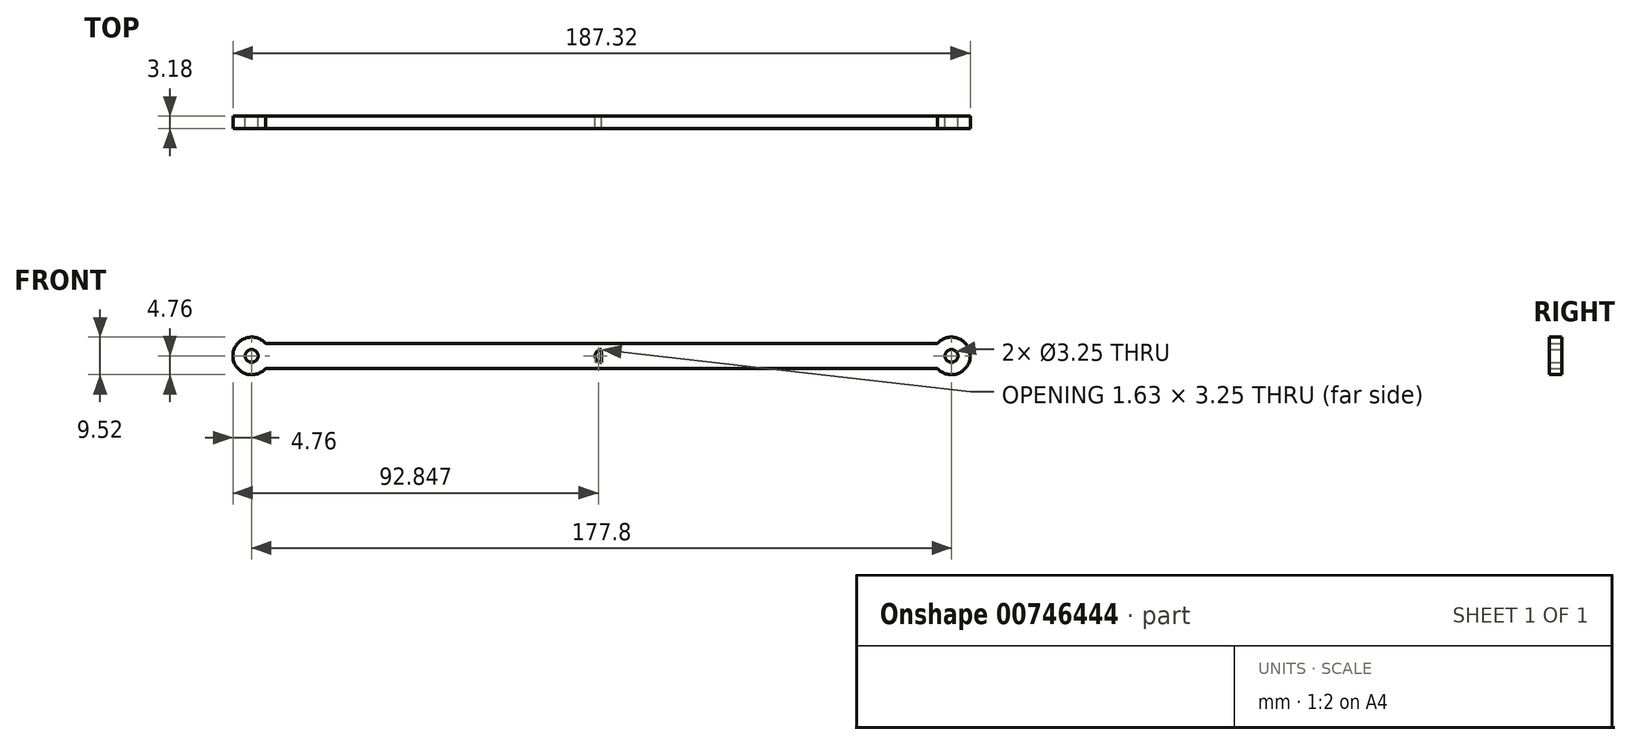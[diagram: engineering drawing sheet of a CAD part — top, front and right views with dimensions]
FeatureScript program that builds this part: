
annotation { "Feature Type Name" : "Feature", "Feature Type Description" : "" }
export const myFeature = defineFeature(function(context is Context, id is Id, definition is map)
    precondition{}
    {
        {
            var Q0;
            Q0=qCreatedBy(makeId("Front.planeOp"),FACE);
            var sketch = newSketch(context, id + "F0", { "sketchPlane" : qUnion([Q0])});
            skLineSegment(sketch, "E0", {"start": v(0, 0) * mm, "end": v(44.45, 0) * mm});
            skCircle(sketch, "E1", {"center": v(44.45, 0) * mm, "radius": 1.63 * mm});
            skArc(sketch, "E2", {"start": v(40.9, -3.17) * mm, "mid": v(49.21, 0) * mm, "end": v(40.9, 3.18) * mm});
            skLineSegment(sketch, "E3.0", {"start": v(0, -3.18) * mm, "end": v(40.9, -3.18) * mm});
            skLineSegment(sketch, "E4.0", {"start": v(0, 3.18) * mm, "end": v(40.9, 3.18) * mm});
            skLineSegment(sketch, "E5", {"start": v(0, 3.18) * mm, "end": v(0, -3.18) * mm});
            skLineSegment(sketch, "E6.MirrorCS", {"start": v(0, 3.18) * mm, "end": v(-48, 3.18) * mm});
            skArc(sketch, "E7.MirrorCS", {"start": v(-40.9, -3.17) * mm, "mid": v(-49.21, 0) * mm, "end": v(-40.9, 3.18) * mm});
            skCircle(sketch, "E8.MirrorC", {"center": v(-44.45, 0) * mm, "radius": 1.63 * mm});
            skLineSegment(sketch, "E9.MirrorCS", {"start": v(0, -3.18) * mm, "end": v(-48, -3.18) * mm});
            skLineSegment(sketch, "E10", {"start": v(-44.45, 4.76) * mm, "end": v(-44.45, -4.76) * mm});
            skLineSegment(sketch, "E11.MirrorCS", {"start": v(-88.9, 3.18) * mm, "end": v(-48, 3.18) * mm});
            skLineSegment(sketch, "E12.MirrorCS", {"start": v(-88.9, -3.18) * mm, "end": v(-48, -3.18) * mm});
            skLineSegment(sketch, "E13.MirrorCS", {"start": v(-88.9, -3.18) * mm, "end": v(-129.8, -3.18) * mm});
            skLineSegment(sketch, "E14.MirrorCS", {"start": v(-88.9, 3.18) * mm, "end": v(-129.8, 3.18) * mm});
            skArc(sketch, "E15.MirrorCS", {"start": v(-129.8, -3.17) * mm, "mid": v(-138.11, 0) * mm, "end": v(-129.8, 3.18) * mm});
            skCircle(sketch, "E16.MirrorC", {"center": v(-133.35, 0) * mm, "radius": 1.63 * mm});
            skPoint(sketch, "E17.orphan", {"position": v(-40.9, 3.18) * mm});
            skPoint(sketch, "E18.orphan", {"position": v(-40.9, -3.18) * mm});
            skSolve(sketch);
        }
        {
            var Q0;
            {var subQ0=sQuery(id+"F0.wireOp",EDGE,"E6.MirrorCS");Q0=makeQuery(id+"F0.imprint","IMPRINT",FACE,{"disambiguationData":[TD([[makeQuery(id+"F0.imprint","IMPRINT",EDGE,{"derivedFrom":subQ0}),1.0]])]});}
            var Q1;
            Q1=makeQuery(id+"F0.imprint","IMPRINT",FACE,{"disambiguationData":[TD([[makeQuery(id+"F0.imprint","IMPRINT",EDGE,{"derivedFrom":sQuery(id+"F0.wireOp",EDGE,"E1")}),-1.0]])]});
            var Q2;
            {var subQ0=sQuery(id+"F0.wireOp",EDGE,"E11.MirrorCS");Q2=makeQuery(id+"F0.imprint","IMPRINT",FACE,{"disambiguationData":[TD([[makeQuery(id+"F0.imprint","IMPRINT",EDGE,{"derivedFrom":subQ0}),-1.0]])]});}
            var Q3;
            {var subQ0=sQuery(id+"F0.wireOp",EDGE,"E10");var subQ1=sQuery(id+"F0.wireOp",EDGE,"E8.MirrorC");var subQ2=makeQuery(id+"F0.imprint","INTERSECT",VERTEX,{"disambiguationData":[OD(0.0)],"derivedFrom":[subQ1,subQ0]});Q3=makeQuery(id+"F0.imprint","IMPRINT",FACE,{"disambiguationData":[TD([[makeQuery(id+"F0.imprint","IMPRINT",EDGE,{"disambiguationData":[TD([[subQ2,1.0]])],"derivedFrom":subQ1}),1.0]])]});}
            var Q4;
            {var subQ0=sQuery(id+"F0.wireOp",EDGE,"E10");var subQ1=sQuery(id+"F0.wireOp",EDGE,"E8.MirrorC");var subQ2=makeQuery(id+"F0.imprint","INTERSECT",VERTEX,{"disambiguationData":[OD(0.0)],"derivedFrom":[subQ1,subQ0]});Q4=makeQuery(id+"F0.imprint","IMPRINT",FACE,{"disambiguationData":[TD([[makeQuery(id+"F0.imprint","IMPRINT",EDGE,{"disambiguationData":[TD([[subQ2,1.0]])],"derivedFrom":subQ1}),-1.0]])]});}
            var Q5;
            {var subQ0=sQuery(id+"F0.wireOp",EDGE,"E10");var subQ1=sQuery(id+"F0.wireOp",EDGE,"E8.MirrorC");var subQ2=makeQuery(id+"F0.imprint","INTERSECT",VERTEX,{"disambiguationData":[OD(0.0)],"derivedFrom":[subQ1,subQ0]});Q5=makeQuery(id+"F0.imprint","IMPRINT",FACE,{"disambiguationData":[TD([[makeQuery(id+"F0.imprint","IMPRINT",EDGE,{"disambiguationData":[TD([[subQ2,-1.0]])],"derivedFrom":subQ1}),-1.0]])]});}
            extrude(context, id + "F1", {"entities" : qUnion([Q0, Q1, Q2, Q3, Q4, Q5]), "depth" : 3.17 * mm, "offsetDistance" : 25.4 * mm});
        }
    });
